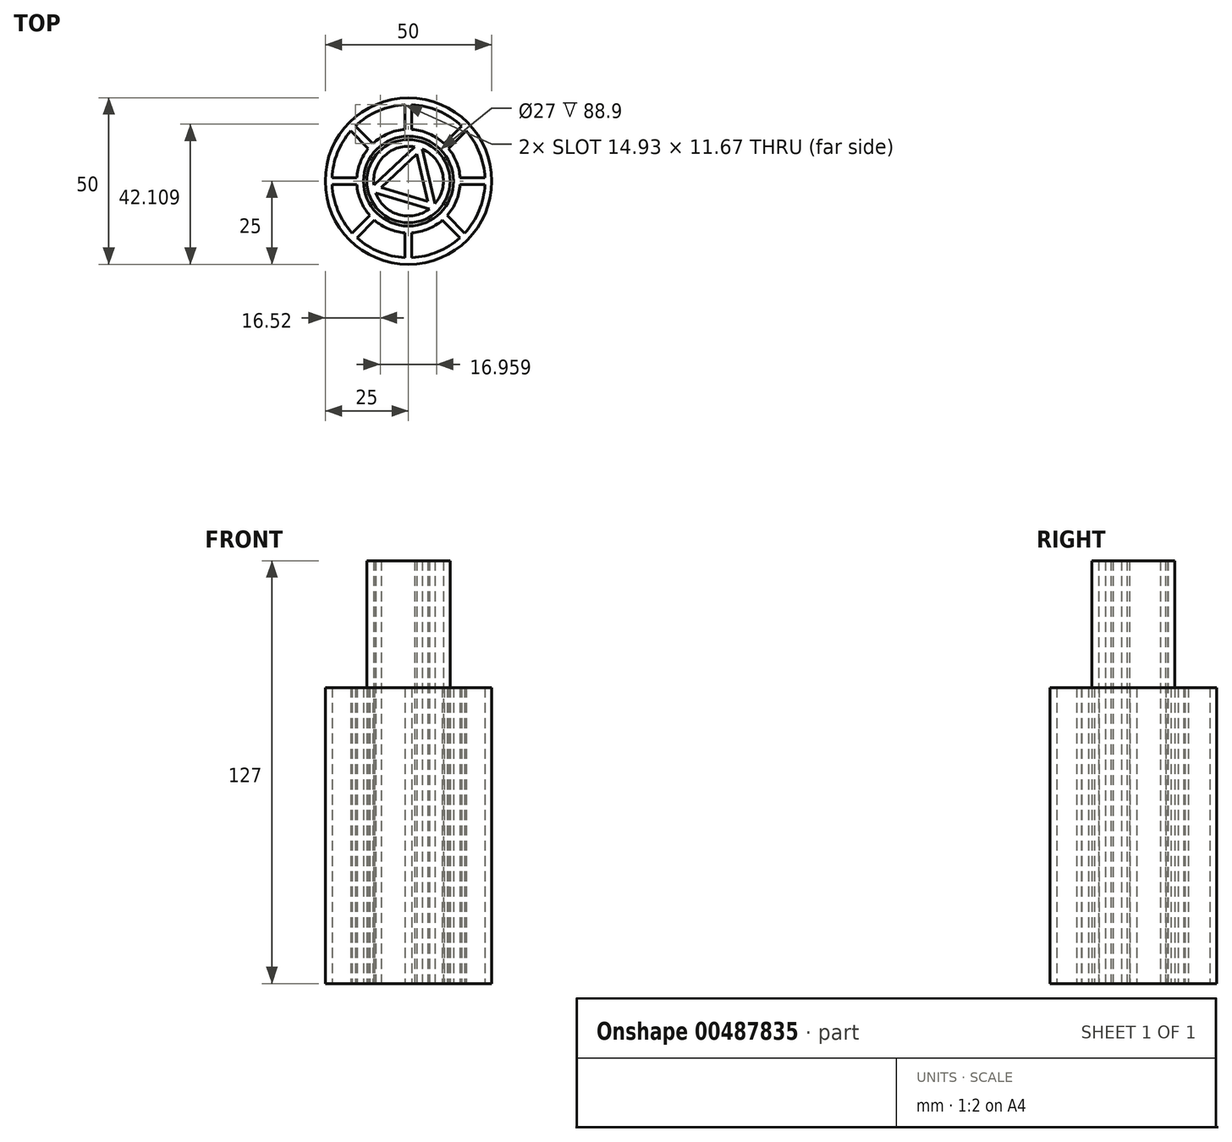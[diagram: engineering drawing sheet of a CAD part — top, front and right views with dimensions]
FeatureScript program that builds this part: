
annotation { "Feature Type Name" : "Feature", "Feature Type Description" : "" }
export const myFeature = defineFeature(function(context is Context, id is Id, definition is map)
    precondition{}
    {
        {
            var Q0;
            Q0=qCreatedBy(makeId("Top.planeOp"),FACE);
            var sketch = newSketch(context, id + "F0", { "sketchPlane" : qUnion([Q0])});
            skCircle(sketch, "E0", {"center": v(0, 0) * mm, "radius": 12.5 * mm});
            skCircle(sketch, "E1.0", {"center": v(0, 0) * mm, "radius": 10.47 * mm});
            skCircle(sketch, "E2.0", {"center": v(0, 0) * mm, "radius": 13.5 * mm});
            skCircle(sketch, "E3.0", {"center": v(0, 0) * mm, "radius": 15.53 * mm});
            skArc(sketch, "E4.cCircle", {"start": v(8.01, -6.74) * mm, "mid": v(-7.18, 7.62) * mm, "end": v(6.24, -8.4) * mm, "construction": true});
            skCircle(sketch, "E5.cCircle", {"center": v(0, 0) * mm, "radius": 12.5 * mm, "construction": true});
            skLineSegment(sketch, "E5.0", {"start": v(4.16, 9.6) * mm, "end": v(8.01, -6.74) * mm});
            skLineSegment(sketch, "E5.1", {"start": v(6.24, -8.4) * mm, "end": v(-9.84, -3.57) * mm});
            skLineSegment(sketch, "E5.2", {"start": v(-10.4, -1.2) * mm, "end": v(1.83, 10.3) * mm});
            skLineSegment(sketch, "E6.0", {"start": v(-8.21, -1.94) * mm, "end": v(2.43, 8.08) * mm});
            skLineSegment(sketch, "E6.1", {"start": v(5.78, -6.14) * mm, "end": v(-8.21, -1.94) * mm});
            skLineSegment(sketch, "E6.2", {"start": v(2.43, 8.08) * mm, "end": v(5.78, -6.14) * mm});
            skLineSegment(sketch, "E7.bottom", {"start": v(-15.5, -1.02) * mm, "end": v(-24.98, -1.02) * mm});
            skLineSegment(sketch, "E7.top", {"start": v(-15.5, 1.02) * mm, "end": v(-24.98, 1.02) * mm});
            skPoint(sketch, "E7.middle", {"position": v(-20.74, 0) * mm});
            skLineSegment(sketch, "E8.bottom", {"start": v(-12.07, 9.78) * mm, "end": v(-18.78, 16.5) * mm});
            skLineSegment(sketch, "E8.top", {"start": v(-10.68, 11.27) * mm, "end": v(-17.38, 17.97) * mm});
            skPoint(sketch, "E8.middle", {"position": v(-10.32, 13.44) * mm});
            skLineSegment(sketch, "E9.bottom", {"start": v(-10.17, -11.74) * mm, "end": v(-16.87, -18.45) * mm});
            skLineSegment(sketch, "E9.top", {"start": v(-11.61, -10.31) * mm, "end": v(-18.32, -17.02) * mm});
            skPoint(sketch, "E9.middle", {"position": v(-15.1, -16.59) * mm});
            skLineSegment(sketch, "E10.MirrorCS", {"start": v(10.17, -11.74) * mm, "end": v(16.87, -18.45) * mm});
            skLineSegment(sketch, "E11.MirrorCS", {"start": v(11.61, -10.31) * mm, "end": v(18.32, -17.02) * mm});
            skLineSegment(sketch, "E12.MirrorCS", {"start": v(15.5, -1.02) * mm, "end": v(24.98, -1.02) * mm});
            skLineSegment(sketch, "E13.MirrorCS", {"start": v(15.5, 1.02) * mm, "end": v(24.98, 1.02) * mm});
            skLineSegment(sketch, "E14.MirrorCS", {"start": v(10.68, 11.27) * mm, "end": v(17.38, 17.97) * mm});
            skLineSegment(sketch, "E15.MirrorCS", {"start": v(12.07, 9.78) * mm, "end": v(18.78, 16.5) * mm});
            skLineSegment(sketch, "E16.left", {"start": v(1.02, -24.98) * mm, "end": v(1.02, -15.5) * mm});
            skLineSegment(sketch, "E16.right", {"start": v(-1.02, -24.98) * mm, "end": v(-1.02, -15.5) * mm});
            skPoint(sketch, "E16.middle", {"position": v(0, -20.3) * mm});
            skLineSegment(sketch, "E17.left", {"start": v(1.02, 15.5) * mm, "end": v(1.02, 24.98) * mm});
            skLineSegment(sketch, "E17.right", {"start": v(-1.02, 15.5) * mm, "end": v(-1.02, 24.98) * mm});
            skPoint(sketch, "E17.middle", {"position": v(0, 20.14) * mm});
            skPoint(sketch, "E18.orphan", {"position": v(-12.17, -2.87) * mm});
            skPoint(sketch, "E19.orphan", {"position": v(8.57, -9.1) * mm});
            skPoint(sketch, "E20.orphan", {"position": v(3.6, 11.97) * mm});
            skPoint(sketch, "E21.MirrorCS.end.orphan", {"position": v(9.86, 10.44) * mm});
            skPoint(sketch, "E21.MirrorCS.start.orphan", {"position": v(11.3, 9) * mm});
            skArc(sketch, "E22", {"start": v(-24.98, 1.02) * mm, "mid": v(-25, 0) * mm, "end": v(-24.98, -1.02) * mm});
            skArc(sketch, "E23", {"start": v(-24.98, -1.02) * mm, "mid": v(25, 0) * mm, "end": v(-24.98, 1.02) * mm});
            skPoint(sketch, "E7.right.end.orphan", {"position": v(-26.45, 1.02) * mm});
            skPoint(sketch, "E24.orphan", {"position": v(-26.45, -1.02) * mm});
            skPoint(sketch, "E25.orphan", {"position": v(-17.94, 18.53) * mm});
            skPoint(sketch, "E26.orphan", {"position": v(-19.37, 17.1) * mm});
            skPoint(sketch, "E27.orphan", {"position": v(-11.3, 9) * mm});
            skPoint(sketch, "E28.orphan", {"position": v(-9.86, 10.44) * mm});
            skPoint(sketch, "E29.orphan", {"position": v(-15.02, 1.02) * mm});
            skPoint(sketch, "E30.orphan", {"position": v(-15.02, -1.02) * mm});
            skPoint(sketch, "E9.left.end.orphan", {"position": v(-10.87, -9.57) * mm});
            skPoint(sketch, "E31.orphan", {"position": v(-9.44, -11.01) * mm});
            skPoint(sketch, "E32.orphan", {"position": v(-18.96, -17.66) * mm});
            skPoint(sketch, "E33.orphan", {"position": v(-17.52, -19.1) * mm});
            skPoint(sketch, "E16.bottom.end.orphan", {"position": v(-1.02, -26.01) * mm});
            skPoint(sketch, "E16.bottom.start.orphan", {"position": v(1.02, -26.01) * mm});
            skPoint(sketch, "E34.orphan", {"position": v(-1.02, -14.58) * mm});
            skPoint(sketch, "E35.orphan", {"position": v(1.02, -14.58) * mm});
            skPoint(sketch, "E36.MirrorCS.start.orphan", {"position": v(9.44, -11.01) * mm});
            skPoint(sketch, "E37.orphan", {"position": v(10.87, -9.57) * mm});
            skPoint(sketch, "E38.MirrorCS.end.orphan", {"position": v(18.96, -17.66) * mm});
            skPoint(sketch, "E38.MirrorCS.start.orphan", {"position": v(17.52, -19.1) * mm});
            skPoint(sketch, "E39.MirrorCS.start.orphan", {"position": v(26.45, -1.02) * mm});
            skPoint(sketch, "E40.orphan", {"position": v(26.45, 1.02) * mm});
            skPoint(sketch, "E41.orphan", {"position": v(17.94, 18.53) * mm});
            skPoint(sketch, "E42.orphan", {"position": v(19.37, 17.1) * mm});
            skPoint(sketch, "E43.orphan", {"position": v(1.02, 25.86) * mm});
            skPoint(sketch, "E44.orphan", {"position": v(-1.02, 25.86) * mm});
            skPoint(sketch, "E17.bottom.start.orphan", {"position": v(1.02, 14.43) * mm});
            skPoint(sketch, "E45.orphan", {"position": v(-1.02, 14.43) * mm});
            skPoint(sketch, "E46.MirrorCS.end.orphan", {"position": v(15.02, 1.02) * mm});
            skPoint(sketch, "E47.orphan", {"position": v(15.02, -1.02) * mm});
            skArc(sketch, "E48.0", {"start": v(-22.95, -0.93) * mm, "mid": v(22.97, 0) * mm, "end": v(-22.95, 0.93) * mm});
            skSolve(sketch);
        }
        {
            var Q0;
            Q0=makeQuery(id+"F0.imprint","IMPRINT",FACE,{"disambiguationData":[TD([[makeQuery(id+"F0.imprint","IMPRINT",EDGE,{"derivedFrom":sQuery(id+"F0.wireOp",EDGE,"E2.0")}),-1.0]])]});
            var Q1;
            {var subQ0=sQuery(id+"F0.wireOp",EDGE,"E8.bottom");Q1=makeQuery(id+"F0.imprint","IMPRINT",FACE,{"disambiguationData":[TD([[makeQuery(id+"F0.imprint","IMPRINT",EDGE,{"derivedFrom":subQ0}),-1.0]])]});}
            var Q2;
            Q2=makeQuery(id+"F0.imprint","IMPRINT",FACE,{"disambiguationData":[TD([[makeQuery(id+"F0.imprint","IMPRINT",EDGE,{"derivedFrom":sQuery(id+"F0.wireOp",EDGE,"c28eb799-c67a-45f2-a46a-9df7d0e12162.0")}),1.0]])]});
            var Q3;
            {var subQ0=sQuery(id+"F0.wireOp",EDGE,"E7.bottom");Q3=makeQuery(id+"F0.imprint","IMPRINT",FACE,{"disambiguationData":[TD([[makeQuery(id+"F0.imprint","IMPRINT",EDGE,{"derivedFrom":subQ0}),-1.0]])]});}
            var Q4;
            {var subQ0=sQuery(id+"F0.wireOp",EDGE,"E14.MirrorCS");Q4=makeQuery(id+"F0.imprint","IMPRINT",FACE,{"disambiguationData":[TD([[makeQuery(id+"F0.imprint","IMPRINT",EDGE,{"derivedFrom":subQ0}),-1.0]])]});}
            var Q5;
            {var subQ0=sQuery(id+"F0.wireOp",EDGE,"E12.MirrorCS");Q5=makeQuery(id+"F0.imprint","IMPRINT",FACE,{"disambiguationData":[TD([[makeQuery(id+"F0.imprint","IMPRINT",EDGE,{"derivedFrom":subQ0}),1.0]])]});}
            var Q6;
            {var subQ0=sQuery(id+"F0.wireOp",EDGE,"E17.left");Q6=makeQuery(id+"F0.imprint","IMPRINT",FACE,{"disambiguationData":[TD([[makeQuery(id+"F0.imprint","IMPRINT",EDGE,{"derivedFrom":subQ0}),1.0]])]});}
            var Q7;
            {var subQ0=sQuery(id+"F0.wireOp",EDGE,"E16.left");Q7=makeQuery(id+"F0.imprint","IMPRINT",FACE,{"disambiguationData":[TD([[makeQuery(id+"F0.imprint","IMPRINT",EDGE,{"derivedFrom":subQ0}),1.0]])]});}
            var Q8;
            {var subQ0=sQuery(id+"F0.wireOp",EDGE,"E9.bottom");Q8=makeQuery(id+"F0.imprint","IMPRINT",FACE,{"disambiguationData":[TD([[makeQuery(id+"F0.imprint","IMPRINT",EDGE,{"derivedFrom":subQ0}),-1.0]])]});}
            var Q9;
            {var subQ0=sQuery(id+"F0.wireOp",EDGE,"E10.MirrorCS");Q9=makeQuery(id+"F0.imprint","IMPRINT",FACE,{"disambiguationData":[TD([[makeQuery(id+"F0.imprint","IMPRINT",EDGE,{"derivedFrom":subQ0}),1.0]])]});}
            var Q10;
            {var subQ0=sQuery(id+"F0.wireOp",EDGE,"E23");var subQ1=sQuery(id+"F0.wireOp",EDGE,"E10.MirrorCS");var subQ2=makeQuery(id+"F0.imprint","INTERSECT",VERTEX,{"derivedFrom":[subQ1,subQ0]});Q10=makeQuery(id+"F0.imprint","IMPRINT",FACE,{"disambiguationData":[TD([[makeQuery(id+"F0.imprint","IMPRINT",EDGE,{"disambiguationData":[TD([[subQ2,1.0]])],"derivedFrom":subQ1}),-1.0]])]});}
            var Q11;
            {var subQ0=sQuery(id+"F0.wireOp",EDGE,"E23");var subQ1=sQuery(id+"F0.wireOp",EDGE,"E11.MirrorCS");var subQ2=makeQuery(id+"F0.imprint","INTERSECT",VERTEX,{"derivedFrom":[subQ1,subQ0]});Q11=makeQuery(id+"F0.imprint","IMPRINT",FACE,{"disambiguationData":[TD([[makeQuery(id+"F0.imprint","IMPRINT",EDGE,{"disambiguationData":[TD([[subQ2,1.0]])],"derivedFrom":subQ1}),1.0]])]});}
            var Q12;
            {var subQ0=sQuery(id+"F0.wireOp",EDGE,"E23");var subQ1=sQuery(id+"F0.wireOp",EDGE,"E13.MirrorCS");var subQ2=makeQuery(id+"F0.imprint","INTERSECT",VERTEX,{"derivedFrom":[subQ1,subQ0]});Q12=makeQuery(id+"F0.imprint","IMPRINT",FACE,{"disambiguationData":[TD([[makeQuery(id+"F0.imprint","IMPRINT",EDGE,{"disambiguationData":[TD([[subQ2,1.0]])],"derivedFrom":subQ1}),1.0]])]});}
            var Q13;
            {var subQ0=sQuery(id+"F0.wireOp",EDGE,"E23");var subQ1=sQuery(id+"F0.wireOp",EDGE,"E9.bottom");var subQ2=makeQuery(id+"F0.imprint","INTERSECT",VERTEX,{"derivedFrom":[subQ1,subQ0]});Q13=makeQuery(id+"F0.imprint","IMPRINT",FACE,{"disambiguationData":[TD([[makeQuery(id+"F0.imprint","IMPRINT",EDGE,{"disambiguationData":[TD([[subQ2,1.0]])],"derivedFrom":subQ1}),1.0]])]});}
            var Q14;
            {var subQ0=sQuery(id+"F0.wireOp",EDGE,"E23");var subQ5=sQuery(id+"F0.wireOp",EDGE,"E9.top");var subQ6=makeQuery(id+"F0.imprint","INTERSECT",VERTEX,{"derivedFrom":[subQ5,subQ0]});Q14=makeQuery(id+"F0.imprint","IMPRINT",FACE,{"disambiguationData":[TD([[makeQuery(id+"F0.imprint","IMPRINT",EDGE,{"disambiguationData":[TD([[subQ6,1.0]])],"derivedFrom":subQ5}),-1.0]])]});}
            var Q15;
            {var subQ0=sQuery(id+"F0.wireOp",EDGE,"E23");var subQ5=sQuery(id+"F0.wireOp",EDGE,"E8.bottom");var subQ6=makeQuery(id+"F0.imprint","INTERSECT",VERTEX,{"derivedFrom":[subQ5,subQ0]});Q15=makeQuery(id+"F0.imprint","IMPRINT",FACE,{"disambiguationData":[TD([[makeQuery(id+"F0.imprint","IMPRINT",EDGE,{"disambiguationData":[TD([[subQ6,1.0]])],"derivedFrom":subQ5}),1.0]])]});}
            var Q16;
            {var subQ0=sQuery(id+"F0.wireOp",EDGE,"E23");var subQ1=sQuery(id+"F0.wireOp",EDGE,"E8.top");var subQ2=makeQuery(id+"F0.imprint","INTERSECT",VERTEX,{"derivedFrom":[subQ1,subQ0]});Q16=makeQuery(id+"F0.imprint","IMPRINT",FACE,{"disambiguationData":[TD([[makeQuery(id+"F0.imprint","IMPRINT",EDGE,{"disambiguationData":[TD([[subQ2,1.0]])],"derivedFrom":subQ1}),-1.0]])]});}
            var Q17;
            {var subQ0=sQuery(id+"F0.wireOp",EDGE,"E23");var subQ1=sQuery(id+"F0.wireOp",EDGE,"E14.MirrorCS");var subQ2=makeQuery(id+"F0.imprint","INTERSECT",VERTEX,{"derivedFrom":[subQ1,subQ0]});Q17=makeQuery(id+"F0.imprint","IMPRINT",FACE,{"disambiguationData":[TD([[makeQuery(id+"F0.imprint","IMPRINT",EDGE,{"disambiguationData":[TD([[subQ2,1.0]])],"derivedFrom":subQ1}),1.0]])]});}
            extrude(context, id + "F1", {"entities" : qUnion([Q0, Q1, Q2, Q3, Q4, Q5, Q6, Q7, Q8, Q9, Q10, Q11, Q12, Q13, Q14, Q15, Q16, Q17]), "oppositeDirection" : true, "depth" : -88.9 * mm});
        }
        {
            var Q0;
            Q0=makeQuery(id+"F0.imprint","IMPRINT",FACE,{"disambiguationData":[TD([[makeQuery(id+"F0.imprint","IMPRINT",EDGE,{"derivedFrom":sQuery(id+"F0.wireOp",EDGE,"E0")}),1.0]])]});
            var Q1;
            {var subQ0=sQuery(id+"F0.wireOp",EDGE,"E5.0");Q1=makeQuery(id+"F0.imprint","IMPRINT",FACE,{"disambiguationData":[TD([[makeQuery(id+"F0.imprint","IMPRINT",EDGE,{"derivedFrom":subQ0}),-1.0]])]});}
            extrude(context, id + "F2", {"entities" : qUnion([Q0, Q1]), "depth" : 127 * mm});
        }
    });
